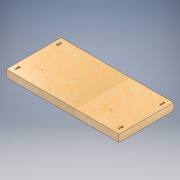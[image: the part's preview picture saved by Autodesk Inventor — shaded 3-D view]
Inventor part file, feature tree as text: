
AUTODESK INVENTOR PART (.ipt)
format: ipt  version: 2022.2 (Build 262287010, 287A)  size: 287,232 bytes
history: native  units: in
note: dims shown in document units (in); Inventor stores cm internally (conversion verified against a paired STEP export)
features: other x15, revolve x6, sketch x4, extrude x1, projected_geometry x1
ambient origin geometry x8: Origin, YZ Plane, XZ Plane, XY Plane, X Axis, Y Axis, Z Axis, Center Point
bodies: Solid1 (feature_tree)
feature tree (27):
  other  "A soffit"
  other  "Blocks"
  extrude  "Extrusion1"  Depth=23.0in
  sketch  "Sketch2"  dims[d2=47.375in d3=0.0in d4=2.0in]
  revolve  "Revolution1"  [1 undecoded]
  revolve  "Revolution2"  Angle=90.0deg
  sketch  "Sketch3"  dims[d5=1.0in d6=90.0deg]
  revolve  "Revolution3"  Angle=90.0deg
  revolve  "Revolution4"  Angle=90.0deg
  sketch  "Sketch4"  dims[d7=90.0deg d8=90.0deg d9=90.0deg d10=90.0deg d11=90.0deg]
  revolve  "Revolution5"  Angle=90.0deg
  revolve  "Revolution6"  Angle=90.0deg
  sketch  "Sketch1"  dims[d0=2.0in d1=23.0in]
  projected_geometry  "Projected Loop1"
  other  "Bolt"
  other  "Block2"
  other  "Block3"
  other  "Block2:1"
  other  "Bolt:2"
  other  "Block2:2"
  other  "Block2:4"
  other  "Block3:1"
  other  "Block3:2"
  other  "Block3:3"
  other  "Block3:4"
  other  "Block3:5"
  other  "Block3:6"
note: 1 required parameter value undecoded (feature->parameter linkage not recoverable at this tier; creation-order binding heuristic only, values carry confidence <= 0.55)
